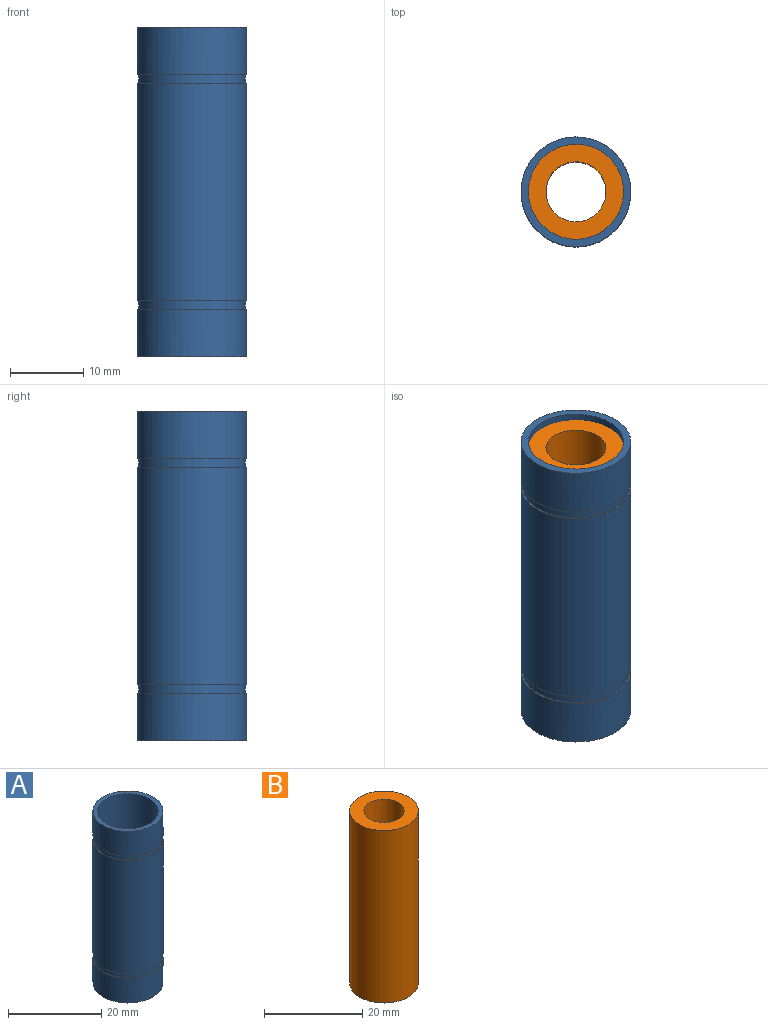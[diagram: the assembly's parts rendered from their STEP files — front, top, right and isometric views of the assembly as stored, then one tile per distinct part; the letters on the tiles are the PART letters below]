
ASSEMBLY  parts=2 mates=1
PART A: 12 faces, bbox 15x15x45 mm
  f0: cylinder r=7.5mm len=15mm, axis (0,0,-1), area 306.3mm2, adj f4,f10
  f1: cylinder r=6.5mm len=45mm, axis (0,0,-1), area 1837.8mm2, adj f3,f4
  f2: cylinder r=7.5mm len=15mm, axis (0,0,-1), area 306.3mm2, adj f3,f7
  f3: plane 15x15mm, normal (0,0,1), area 44mm2, adj f1,f2
  f4: plane 15x15mm, normal (0,0,-1), area 44mm2, adj f0,f1
  f5: cylinder r=7.3mm len=14.6mm, axis (0,0,1), area 50.5mm2, adj f6,f7
  f6: plane 15x15mm, normal (0,0,1), area 9.3mm2, adj f5,f8
  f7: plane 15x15mm, normal (0,0,-1), area 9.3mm2, adj f2,f5
  f8: cylinder r=7.5mm len=29.8mm, axis (0,0,-1), area 1404.3mm2, adj f6,f11
  f9: cylinder r=7.3mm len=14.6mm, axis (0,0,1), area 50.5mm2, adj f10,f11
  f10: plane 15x15mm, normal (0,0,1), area 9.3mm2, adj f0,f9
  f11: plane 15x15mm, normal (0,0,-1), area 9.3mm2, adj f8,f9
PART B: 4 faces, bbox 14x14x43 mm
  f0: cylinder r=4.1mm len=43mm, axis (0,0,-1), area 1107.7mm2, adj f2,f3
  f1: cylinder r=7mm len=43mm, axis (0,0,-1), area 1891.2mm2, adj f2,f3
  f2: plane 14x14mm, normal (0,0,1), area 101.1mm2, adj f0,f1
  f3: plane 14x14mm, normal (0,0,-1), area 101.1mm2, adj f0,f1
PLACE A t=(-15.83,-2.55,-12.63)mm
PLACE B t=(-15.83,-2.55,-11.63)mm
MATE fastened B.f1 <-> A.f0  axis (0,0,-1) through (-15.83,-2.55,9.87)mm
